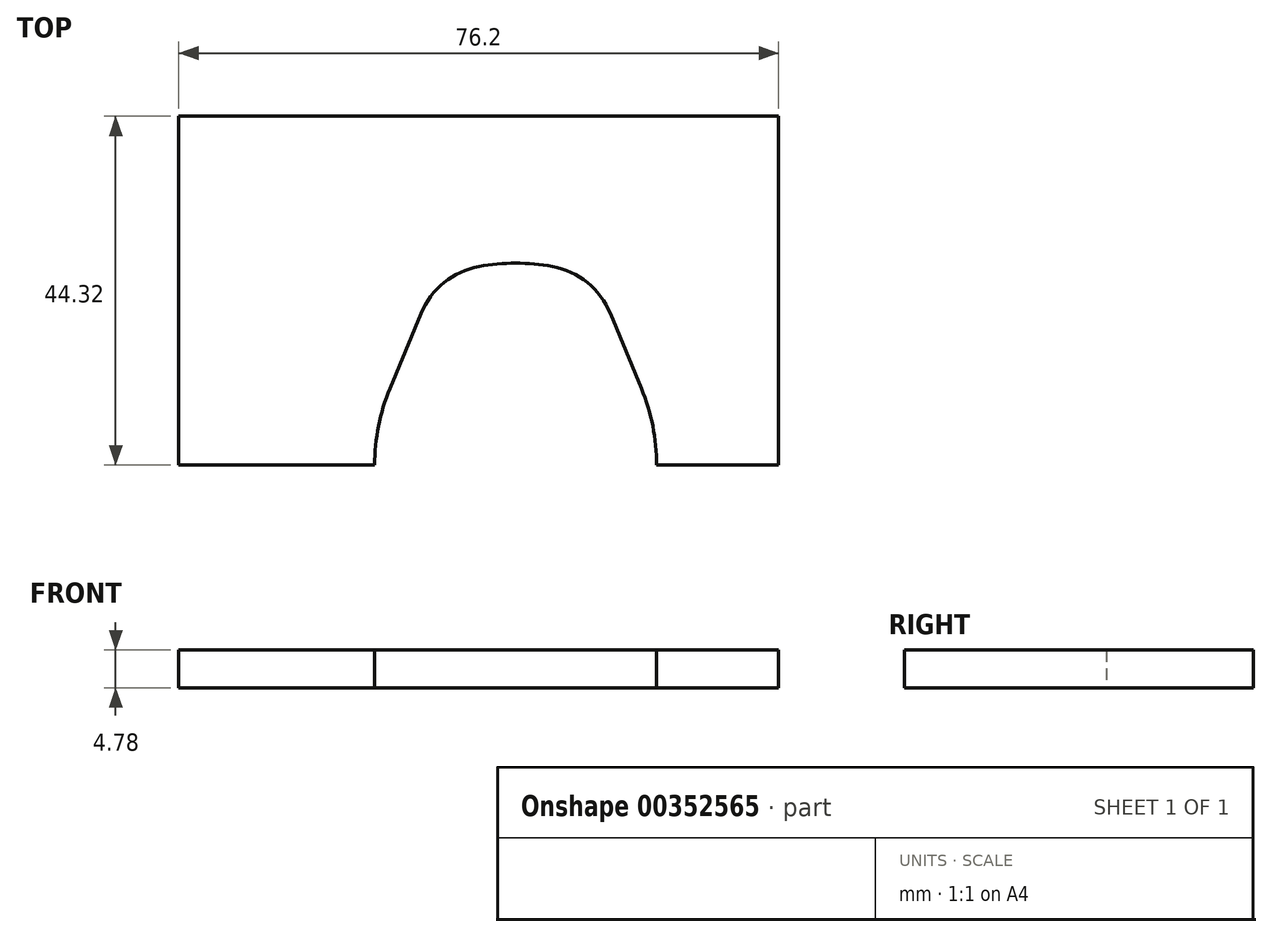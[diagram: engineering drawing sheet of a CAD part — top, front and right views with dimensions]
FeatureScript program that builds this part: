
annotation { "Feature Type Name" : "Feature", "Feature Type Description" : "" }
export const myFeature = defineFeature(function(context is Context, id is Id, definition is map)
    precondition{}
    {
        {
            var Q0;
            Q0=qCreatedBy(makeId("Top.planeOp"),FACE);
            var sketch = newSketch(context, id + "F0", { "sketchPlane" : qUnion([Q0])});
            skLineSegment(sketch, "E0.bottom", {"start": v(-42.8, 44.32) * mm, "end": v(33.4, 44.32) * mm});
            skLineSegment(sketch, "E0.top", {"start": v(-42.8, 0) * mm, "end": v(33.4, 0) * mm});
            skLineSegment(sketch, "E0.left", {"start": v(-42.8, 44.32) * mm, "end": v(-42.8, 0) * mm});
            skLineSegment(sketch, "E0.right", {"start": v(33.4, 44.32) * mm, "end": v(33.4, 0) * mm});
            skLineSegment(sketch, "E1", {"start": v(0, 44.32) * mm, "end": v(0, 0) * mm, "construction": true});
            skArc(sketch, "E2", {"start": v(-15.97, 9.72) * mm, "mid": v(-17.42, 4.96) * mm, "end": v(-17.9, 0) * mm});
            skArc(sketch, "E3", {"start": v(17.9, 0) * mm, "mid": v(17.42, 4.96) * mm, "end": v(15.97, 9.72) * mm});
            skArc(sketch, "E4", {"start": v(4.66, 25.23) * mm, "mid": v(0, 25.65) * mm, "end": v(-4.66, 25.23) * mm});
            skLineSegment(sketch, "E5", {"start": v(-15.97, 9.72) * mm, "end": v(-12.02, 19.28) * mm});
            skLineSegment(sketch, "E6", {"start": v(15.97, 9.72) * mm, "end": v(12.02, 19.28) * mm});
            skPoint(sketch, "E7.visualSharp", {"position": v(10.26, 23.51) * mm});
            skArc(sketch, "E7.filletArc", {"start": v(12.02, 19.28) * mm, "mid": v(9.1, 23.19) * mm, "end": v(4.66, 25.23) * mm});
            skPoint(sketch, "E8.visualSharp", {"position": v(-10.26, 23.51) * mm});
            skArc(sketch, "E8.filletArc", {"start": v(-4.66, 25.23) * mm, "mid": v(-9.1, 23.19) * mm, "end": v(-12.02, 19.28) * mm});
            skSolve(sketch);
        }
        {
            var Q0;
            Q0=makeQuery(id+"F0.imprint","IMPRINT",FACE,{"disambiguationData":[TD([[makeQuery(id+"F0.imprint","IMPRINT",EDGE,{"derivedFrom":sQuery(id+"F0.wireOp",EDGE,"E0.bottom")}),-1.0]])]});
            var Q1;
            {var subQ5=sQuery(id+"F0.wireOp",EDGE,"E6");Q1=makeQuery(id+"F0.imprint","IMPRINT",FACE,{"disambiguationData":[TD([[makeQuery(id+"F0.imprint","IMPRINT",EDGE,{"derivedFrom":subQ5}),-1.0]])]});}
            var Q2;
            {var subQ5=sQuery(id+"F0.wireOp",EDGE,"E5");Q2=makeQuery(id+"F0.imprint","IMPRINT",FACE,{"disambiguationData":[TD([[makeQuery(id+"F0.imprint","IMPRINT",EDGE,{"derivedFrom":subQ5}),1.0]])]});}
            extrude(context, id + "F1", {"entities" : qUnion([Q0, Q1, Q2]), "depth" : 4.78 * mm});
        }
    });
